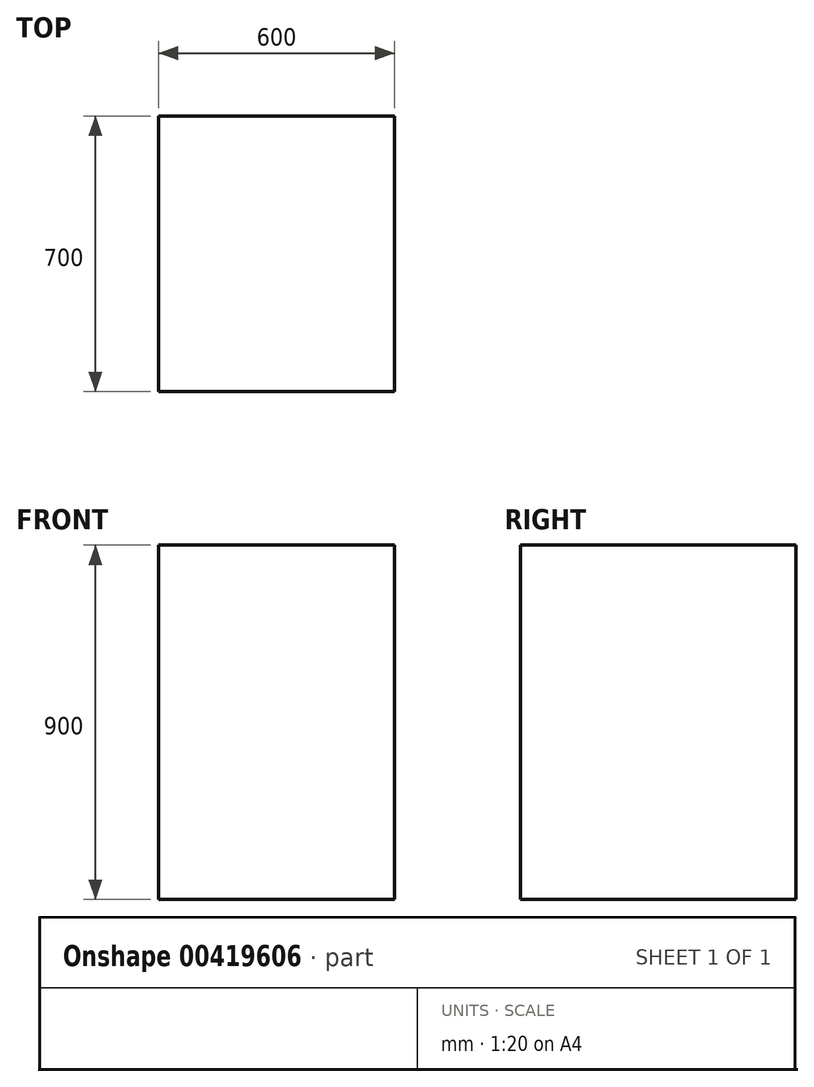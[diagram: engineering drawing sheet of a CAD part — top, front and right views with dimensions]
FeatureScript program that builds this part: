
annotation { "Feature Type Name" : "Feature", "Feature Type Description" : "" }
export const myFeature = defineFeature(function(context is Context, id is Id, definition is map)
    precondition{}
    {
        {
            var Q0;
            Q0=qCreatedBy(makeId("Top.planeOp"),FACE);
            var sketch = newSketch(context, id + "F0", { "sketchPlane" : qUnion([Q0])});
            skLineSegment(sketch, "E0.bottom", {"start": v(-531.3, 657.99) * mm, "end": v(68.7, 657.99) * mm});
            skLineSegment(sketch, "E0.top", {"start": v(-531.3, -42.01) * mm, "end": v(68.7, -42.01) * mm});
            skLineSegment(sketch, "E0.left", {"start": v(-531.3, 657.99) * mm, "end": v(-531.3, -42.01) * mm});
            skLineSegment(sketch, "E0.right", {"start": v(68.7, 657.99) * mm, "end": v(68.7, -42.01) * mm});
            skSolve(sketch);
        }
        {
            var Q0;
            Q0=makeQuery(id+"F0.imprint","IMPRINT",FACE,{"disambiguationData":[TD([[makeQuery(id+"F0.imprint","IMPRINT",EDGE,{"derivedFrom":sQuery(id+"F0.wireOp",EDGE,"E0.bottom")}),-1.0]])]});
            extrude(context, id + "F1", {"entities" : qUnion([Q0]), "depth" : 900 * mm});
        }
    });
